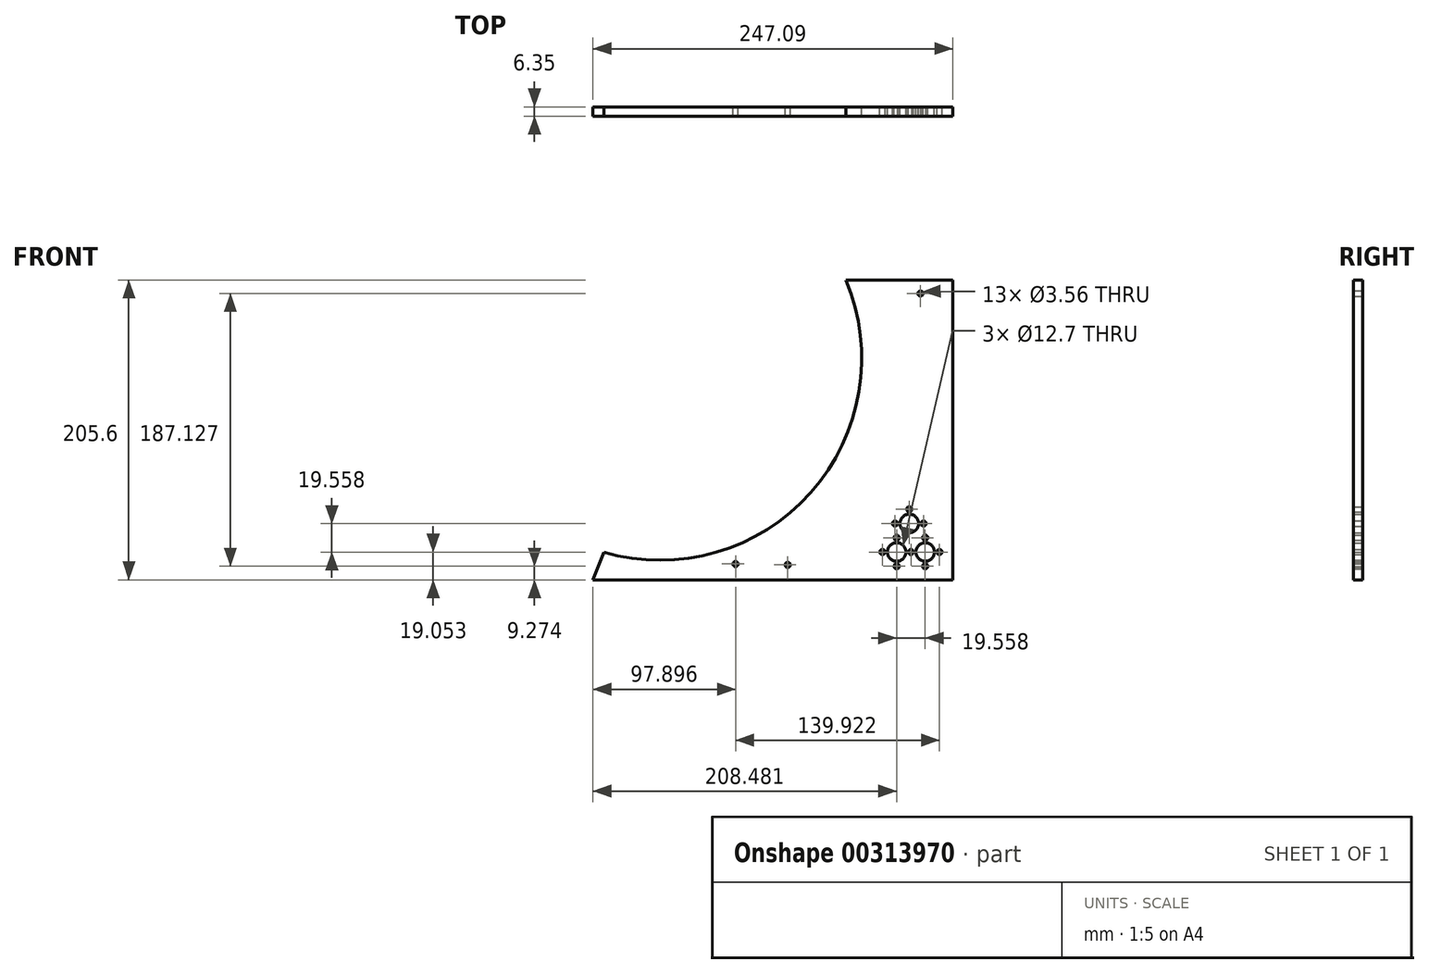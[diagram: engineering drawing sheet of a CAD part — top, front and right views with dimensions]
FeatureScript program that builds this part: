
annotation { "Feature Type Name" : "Feature", "Feature Type Description" : "" }
export const myFeature = defineFeature(function(context is Context, id is Id, definition is map)
    precondition{}
    {
        {
            var Q0;
            Q0=qCreatedBy(makeId("Front.planeOp"),FACE);
            var sketch = newSketch(context, id + "F0", { "sketchPlane" : qUnion([Q0])});
            skArc(sketch, "E0", {"start": v(-38.7, -132.91) * mm, "mid": v(103.39, -92.05) * mm, "end": v(127.55, 53.8) * mm});
            skLineSegment(sketch, "E1", {"start": v(200.99, -145.45) * mm, "end": v(200.99, 53.8) * mm});
            skLineSegment(sketch, "E2", {"start": v(200.99, 53.8) * mm, "end": v(127.55, 53.8) * mm});
            skCircle(sketch, "E3", {"center": v(181.94, -132.75) * mm, "radius": 6.35 * mm});
            skCircle(sketch, "E4", {"center": v(181.94, -122.97) * mm, "radius": 1.78 * mm});
            skCircle(sketch, "E5.1.0", {"center": v(172.16, -132.75) * mm, "radius": 1.78 * mm});
            skCircle(sketch, "E5.2.0", {"center": v(181.94, -142.53) * mm, "radius": 1.78 * mm});
            skCircle(sketch, "E5.3.0", {"center": v(191.72, -132.75) * mm, "radius": 1.78 * mm});
            skCircle(sketch, "E6.MirrorC", {"center": v(162.38, -132.75) * mm, "radius": 6.35 * mm});
            skCircle(sketch, "E7.MirrorC", {"center": v(51.8, -140.99) * mm, "radius": 1.78 * mm});
            skLineSegment(sketch, "E8", {"start": v(200.99, -145.45) * mm, "end": v(200.99, -151.8) * mm});
            skLineSegment(sketch, "E9", {"start": v(200.99, -151.8) * mm, "end": v(-38.62, -151.8) * mm});
            skCircle(sketch, "E10.1.0", {"center": v(162.38, -122.97) * mm, "radius": 1.78 * mm});
            skCircle(sketch, "E10.2.0", {"center": v(152.6, -132.75) * mm, "radius": 1.78 * mm});
            skCircle(sketch, "E10.3.0", {"center": v(162.38, -142.53) * mm, "radius": 1.78 * mm});
            skLineSegment(sketch, "E11", {"start": v(-46.1, -151.8) * mm, "end": v(-38.62, -151.8) * mm});
            skLineSegment(sketch, "E12", {"start": v(-38.7, -132.91) * mm, "end": v(-46.1, -151.8) * mm});
            skCircle(sketch, "E13.MirrorC", {"center": v(87.6, -141.6) * mm, "radius": 1.78 * mm});
            skCircle(sketch, "E14.MirrorC", {"center": v(178.7, 44.6) * mm, "radius": 1.78 * mm});
            skCircle(sketch, "E15.MirrorC", {"center": v(161.24, -113.19) * mm, "radius": 1.78 * mm});
            skCircle(sketch, "E16.MirrorC", {"center": v(171.01, -113.19) * mm, "radius": 6.35 * mm});
            skCircle(sketch, "E17.MirrorC", {"center": v(180.8, -113.19) * mm, "radius": 1.78 * mm});
            skCircle(sketch, "E18.MirrorC", {"center": v(171.01, -103.4) * mm, "radius": 1.78 * mm});
            skSolve(sketch);
        }
        {
            var Q0;
            Q0=makeQuery(id+"F0.imprint","IMPRINT",FACE,{"disambiguationData":[TD([[makeQuery(id+"F0.imprint","IMPRINT",EDGE,{"derivedFrom":sQuery(id+"F0.wireOp",EDGE,"E0")}),-1.0]])]});
            extrude(context, id + "F1", {"entities" : qUnion([Q0]), "depth" : 6.35 * mm});
        }
    });
